FCSTD DOCUMENT  (FreeCAD 0.19R24291 (Git))
Label: Gear_Control_Geometry
License: Creative Commons Attribution-NonCommercial
LicenseURL: http://creativecommons.org/licenses/by-nc/4.0/
objects: TechDraw::DrawViewDimension×9, Sketcher::SketchObject×4, PartDesign::Body×3, TechDraw::DrawViewPart×2, Spreadsheet::Sheet×1, TechDraw::DrawSVGTemplate×1, TechDraw::DrawRichAnno×1, TechDraw::DrawPage×1
note: 7 computed .brp shape members not serialized (recipe doc carries the construction recipe); baked Part::Feature solids carry a one-line shape summary decoded from their .brp

FEATURE [Sketcher::SketchObject] Sketch  label="Frame"
  FullyConstrained = true
  MapMode = 5
  Support = -> [XY_Plane]
  expr: .Constraints.baseLocationX = .Constraints.scale / 2
  expr: .Constraints.baseLocationY = .Constraints.scale / 2
  expr: Constraints[9] = .Constraints.scale
  sketch-geometry (4):
    g0: LineSegment StartX=-107 StartY=107 StartZ=0 EndX=107 EndY=107 EndZ=0
    g1: LineSegment StartX=107 StartY=107 StartZ=0 EndX=107 EndY=-107 EndZ=0
    g2: LineSegment StartX=107 StartY=-107 StartZ=0 EndX=-107 EndY=-107 EndZ=0
    g3: LineSegment StartX=-107 StartY=-107 StartZ=0 EndX=-107 EndY=107 EndZ=0
  constraints (12):
    c: Coincident(g0,g1)
    c: Coincident(g1,g2)
    c: Coincident(g2,g3)
    c: Coincident(g3,g0)
    c: Horizontal(g0)
    c: Horizontal(g2)
    c: Vertical(g1)
    c: Vertical(g3)
    c: DistanceX(g0,g0) = 214  'scale'
    c: DistanceY(g1,g1) = 214
    c: Distance(g0,g-1) = 107  'baseLocationY'
    c: Distance(g0,g-2) = 107  'baseLocationX'
FEATURE [Spreadsheet::Sheet] Spreadsheet
  cells = A1=sepAngule; B1=shiftAngule; A2(sepAngule)==360 / 32; B2(shiftAngle)==sepAngule / 2; A4=points; A5=1; B5(a1)=5.625; A6=2; B6(a2)=16.875; A7=3; B7(a3)=28.125; A8=4; B8(a4)=39.375; A9=5; B9(a5)=50.625; A10=6; B10(a6)=61.875; A11=7; B11(a7)=73.125; A12=8; B12(a8)=84.375; A13=9; B13(a9)=95.625; A14=10; B14(a10)=106.875; A15=11; B15(a11)=118.125; A16=12; B16(a12)=129.375; A17=13; B17(a13)=140.625; A18=14; B18(a14)=151.875; A19=15; B19(a15)=163.125; A20=16; B20(a16)=174.375; A21=17; B21(a17)=185.625; A22=18; B22(a18)=196.875; A23=19; B23(a19)=208.125; A24=20; B24(a20)=219.375; A25=21; B25(a21)=230.625; A26=22; B26(a22)=241.875; A27=23; B27(a23)=253.125; A28=24; B28(a24)=264.375; A29=25; B29(a25)=275.625; A30=26; B30(a26)=286.875; A31=27; B31(a27)=298.125; A32=28; B32(a28)=309.375; A33=29; B33(a29)=320.625; A34=30; B34(a30)=331.875; A35=31; B35(a31)=343.125; A36=32; B36(a32)=354.375
FEATURE [PartDesign::Body] Body001  label="Marker"
  Origin = -> Origin001
FEATURE [Sketcher::SketchObject] Sketch003  label="Positions"
  FullyConstrained = true
  MapMode = 5
  Support = -> [XY_Plane002]
  expr: Constraints[18] = .Constraints.centerPointLenght
  expr: Constraints[19] = .Constraints.centerPointLenght
  expr: Constraints[23] = .Constraints.centerPointLenght
  expr: Constraints[20] = .Constraints.centerPointLenght
  expr: Constraints[21] = .Constraints.centerPointLenght
  expr: Constraints[22] = .Constraints.centerPointLenght
  expr: Constraints[24] = .Constraints.centerPointLenght
  sketch-geometry (16):
    g0: LineSegment StartX=0 StartY=0 StartZ=0 EndX=0 EndY=74 EndZ=0
    g1: GeomPoint X=0 Y=74 Z=0
    g2: LineSegment StartX=0 StartY=0 StartZ=0 EndX=52.3259 EndY=52.3259 EndZ=0
    g3: LineSegment StartX=0 StartY=0 StartZ=0 EndX=-52.3259 EndY=52.3259 EndZ=0
    g4: LineSegment StartX=0 StartY=0 StartZ=0 EndX=74 EndY=0 EndZ=0
    g5: LineSegment StartX=0 StartY=0 StartZ=0 EndX=-74 EndY=0 EndZ=0
    g6: LineSegment StartX=0 StartY=0 StartZ=0 EndX=0 EndY=-74 EndZ=0
    g7: LineSegment StartX=0 StartY=0 StartZ=0 EndX=52.3259 EndY=-52.3259 EndZ=0
    g8: LineSegment StartX=0 StartY=0 StartZ=0 EndX=-52.3259 EndY=-52.3259 EndZ=0
    g9: GeomPoint X=52.3259 Y=52.3259 Z=0
    g10: GeomPoint X=74 Y=0 Z=0
    g11: GeomPoint X=52.3259 Y=-52.3259 Z=0
    g12: GeomPoint X=0 Y=-74 Z=0
    g13: GeomPoint X=-52.3259 Y=-52.3259 Z=0
    g14: GeomPoint X=-74 Y=0 Z=0
    g15: GeomPoint X=-52.3259 Y=52.3259 Z=0
  constraints (32):
    c: Coincident(g0,g-1)
    c: PointOnObject(g0,g-2)
    c: DistanceY(g0,g0) = 74  'centerPointLenght'
    c: Coincident(g1,g0)
    c: Coincident(g2,g-1)
    c: Coincident(g3,g-1)
    c: Coincident(g4,g-1)
    c: PointOnObject(g4,g-1)
    c: Coincident(g5,g-1)
    c: PointOnObject(g5,g-1)
    c: Coincident(g6,g-1)
    c: PointOnObject(g6,g-2)
    c: Coincident(g7,g-1)
    c: Coincident(g8,g-1)
    c: Angle(g8,g6) = 0.785398
    c: Angle(g6,g7) = 0.785398
    c: Angle(g4,g2) = 0.785398
    c: Angle(g3,g5) = 0.785398
    c: Distance(g2) = 74
    c: Distance(g4) = 74
    c: Distance(g7) = 74
    c: Distance(g6) = 74
    c: Distance(g8) = 74
    c: Distance(g5) = 74
    c: Distance(g3) = 74
    c: Coincident(g9,g2)
    c: Coincident(g10,g4)
    c: Coincident(g11,g7)
    c: Coincident(g12,g6)
    c: Coincident(g13,g8)
    c: Coincident(g14,g5)
    c: Coincident(g15,g3)
FEATURE [PartDesign::Body] Body002  label="NumberPosition"
  Group = -> [Sketch003]
  Origin = -> Origin002
FEATURE [TechDraw::DrawSVGTemplate] Template
  Height = 297
  Orientation = 0
  Width = 210
FEATURE [TechDraw::DrawViewPart] View001
  CoarseView = false
  Direction = (0,0,1)
  Focus = 100
  HardHidden = false
  IsoCount = 0
  IsoHidden = false
  IsoVisible = false
  LockPosition = true
  Perspective = false
  Rotation = 0
  ScaleType = 0
  SeamHidden = false
  SeamVisible = true
  SmoothHidden = false
  SmoothVisible = true
  Source = -> [Sketch003]
  X = 105
  XDirection = (1,0,0)
  Y = 148.5
FEATURE [Sketcher::SketchObject] Sketch004  label="Positions001"
  FullyConstrained = true
  MapMode = 5
  Support = -> [XY_Plane]
  expr: Constraints[24] = .Constraints.centerPointLenght
  expr: Constraints[22] = .Constraints.centerPointLenght
  expr: Constraints[21] = .Constraints.centerPointLenght
  expr: Constraints[20] = .Constraints.centerPointLenght
  expr: Constraints[23] = .Constraints.centerPointLenght
  expr: Constraints[19] = .Constraints.centerPointLenght
  expr: Constraints[18] = .Constraints.centerPointLenght
  sketch-geometry (16):
    g0: LineSegment StartX=0 StartY=0 StartZ=0 EndX=0 EndY=74 EndZ=0
    g1: GeomPoint X=0 Y=74 Z=0
    g2: LineSegment StartX=0 StartY=0 StartZ=0 EndX=52.3259 EndY=52.3259 EndZ=0
    g3: LineSegment StartX=0 StartY=0 StartZ=0 EndX=-52.3259 EndY=52.3259 EndZ=0
    g4: LineSegment StartX=0 StartY=0 StartZ=0 EndX=74 EndY=0 EndZ=0
    g5: LineSegment StartX=0 StartY=0 StartZ=0 EndX=-74 EndY=0 EndZ=0
    g6: LineSegment StartX=0 StartY=0 StartZ=0 EndX=0 EndY=-74 EndZ=0
    g7: LineSegment StartX=0 StartY=0 StartZ=0 EndX=52.3259 EndY=-52.3259 EndZ=0
    g8: LineSegment StartX=0 StartY=0 StartZ=0 EndX=-52.3259 EndY=-52.3259 EndZ=0
    g9: GeomPoint X=52.3259 Y=52.3259 Z=0
    g10: GeomPoint X=74 Y=0 Z=0
    g11: GeomPoint X=52.3259 Y=-52.3259 Z=0
    g12: GeomPoint X=0 Y=-74 Z=0
    g13: GeomPoint X=-52.3259 Y=-52.3259 Z=0
    g14: GeomPoint X=-74 Y=0 Z=0
    g15: GeomPoint X=-52.3259 Y=52.3259 Z=0
  constraints (32):
    c: Coincident(g0,g-1)
    c: PointOnObject(g0,g-2)
    c: DistanceY(g0,g0) = 74  'centerPointLenght'
    c: Coincident(g1,g0)
    c: Coincident(g2,g-1)
    c: Coincident(g3,g-1)
    c: Coincident(g4,g-1)
    c: PointOnObject(g4,g-1)
    c: Coincident(g5,g-1)
    c: PointOnObject(g5,g-1)
    c: Coincident(g6,g-1)
    c: PointOnObject(g6,g-2)
    c: Coincident(g7,g-1)
    c: Coincident(g8,g-1)
    c: Angle(g8,g6) = 0.785398
    c: Angle(g6,g7) = 0.785398
    c: Angle(g4,g2) = 0.785398
    c: Angle(g3,g5) = 0.785398
    c: Distance(g2) = 74
    c: Distance(g4) = 74
    c: Distance(g7) = 74
    c: Distance(g6) = 74
    c: Distance(g8) = 74
    c: Distance(g5) = 74
    c: Distance(g3) = 74
    c: Coincident(g9,g2)
    c: Coincident(g10,g4)
    c: Coincident(g11,g7)
    c: Coincident(g12,g6)
    c: Coincident(g13,g8)
    c: Coincident(g14,g5)
    c: Coincident(g15,g3)
FEATURE [Sketcher::SketchObject] Sketch001  label="MainGearSketch"
  ExternalGeometry = -> [Sketch004,Sketch]
  FullyConstrained = true
  MapMode = 5
  Support = -> [XY_Plane]
  expr: Constraints[57] = Spreadsheet.sepAngule
  expr: Constraints[72] = .Constraints.radInt
  expr: Constraints[60] = Spreadsheet.sepAngule
  expr: Constraints[35] = Spreadsheet.sepAngule
  expr: Constraints[33] = Spreadsheet.sepAngule
  expr: Constraints[71] = .Constraints.radInt
  expr: Constraints[69] = .Constraints.radInt
  expr: Constraints[49] = Spreadsheet.sepAngule
  expr: Constraints[58] = Spreadsheet.sepAngule
  expr: Constraints[45] = Spreadsheet.sepAngule
  expr: Constraints[63] = Spreadsheet.sepAngule
  expr: Constraints[112] = .Constraints.radExt
  expr: Constraints[47] = Spreadsheet.sepAngule
  expr: Constraints[111] = .Constraints.radExt
  expr: Constraints[68] = .Constraints.radInt
  expr: Constraints[82] = .Constraints.radExt
  expr: .Constraints.radExt = 91mm
  expr: Constraints[48] = Spreadsheet.sepAngule
  expr: Constraints[64] = Spreadsheet.sepAngule
  expr: Constraints[163] = .Constraints.radExt
  expr: Constraints[110] = .Constraints.radExt
  expr: Constraints[109] = .Constraints.radExt
  expr: Constraints[67] = .Constraints.radInt
  expr: Constraints[43] = Spreadsheet.sepAngule
  expr: .Constraints.p3 = Spreadsheet.sepAngule
  expr: Constraints[34] = Spreadsheet.sepAngule
  expr: .Constraints.p5 = Spreadsheet.sepAngule
  expr: Constraints[26] = Spreadsheet.sepAngule
  expr: Constraints[74] = .Constraints.radInt
  expr: Constraints[32] = Spreadsheet.sepAngule
  expr: Constraints[79] = .Constraints.radExt
  expr: Constraints[78] = .Constraints.radExt
  expr: Constraints[42] = Spreadsheet.sepAngule
  expr: Constraints[81] = .Constraints.radExt
  expr: Constraints[80] = .Constraints.radExt
  expr: .Constraints.p2 = Spreadsheet.sepAngule
  expr: Constraints[61] = Spreadsheet.sepAngule
  expr: .Constraints.p7 = Spreadsheet.sepAngule
  expr: .Constraints.p4 = Spreadsheet.sepAngule
  expr: Constraints[59] = Spreadsheet.sepAngule
  expr: Constraints[73] = .Constraints.radInt
  expr: Constraints[46] = Spreadsheet.sepAngule
  expr: Constraints[27] = Spreadsheet.sepAngule
  expr: Constraints[70] = .Constraints.radInt
  expr: .Constraints.p6 = Spreadsheet.sepAngule
  expr: Constraints[25] = Spreadsheet.sepAngule
  expr: .Constraints.p1 = Spreadsheet.a1
  expr: Constraints[28] = Spreadsheet.sepAngule
  expr: Constraints[30] = Spreadsheet.sepAngule
  expr: Constraints[31] = Spreadsheet.sepAngule
  expr: Constraints[65] = Spreadsheet.sepAngule
  expr: .Constraints.p8 = Spreadsheet.sepAngule
  expr: Constraints[44] = Spreadsheet.sepAngule
  expr: Constraints[29] = Spreadsheet.sepAngule
  expr: Constraints[62] = Spreadsheet.sepAngule
  sketch-geometry (66):
    g0: LineSegment StartX=0 StartY=0 StartZ=0 EndX=0 EndY=91 EndZ=0
    g1: LineSegment StartX=0 StartY=0 StartZ=0 EndX=8.91956 EndY=90.5618 EndZ=0
    g2: LineSegment StartX=0 StartY=0 StartZ=0 EndX=19.8119 EndY=65.3112 EndZ=0
    g3: LineSegment StartX=0 StartY=0 StartZ=0 EndX=32.1728 EndY=60.1911 EndZ=0
    g4: LineSegment StartX=0 StartY=0 StartZ=0 EndX=57.7298 EndY=70.344 EndZ=0
    g5: LineSegment StartX=0 StartY=0 StartZ=0 EndX=70.344 EndY=57.7298 EndZ=0
    g6: LineSegment StartX=0 StartY=0 StartZ=0 EndX=60.1911 EndY=32.1728 EndZ=0
    g7: LineSegment StartX=0 StartY=0 StartZ=0 EndX=65.3112 EndY=19.8119 EndZ=0
    g8: LineSegment StartX=0 StartY=0 StartZ=0 EndX=90.5618 EndY=8.91956 EndZ=0
    g9: LineSegment StartX=0 StartY=0 StartZ=0 EndX=90.5618 EndY=-8.91956 EndZ=0
    g10: LineSegment StartX=0 StartY=0 StartZ=0 EndX=65.3112 EndY=-19.8119 EndZ=0
    g11: LineSegment StartX=0 StartY=0 StartZ=0 EndX=60.1911 EndY=-32.1728 EndZ=0
    g12: LineSegment StartX=0 StartY=0 StartZ=0 EndX=70.344 EndY=-57.7298 EndZ=0
    g13: LineSegment StartX=0 StartY=0 StartZ=0 EndX=57.7298 EndY=-70.344 EndZ=0
    g14: LineSegment StartX=0 StartY=0 StartZ=0 EndX=32.1728 EndY=-60.1911 EndZ=0
    g15: LineSegment StartX=0 StartY=0 StartZ=0 EndX=19.8119 EndY=-65.3112 EndZ=0
    g16: LineSegment StartX=0 StartY=0 StartZ=0 EndX=8.91956 EndY=-90.5618 EndZ=0
    g17: LineSegment StartX=0 StartY=0 StartZ=0 EndX=-8.91956 EndY=-90.5618 EndZ=0
    g18: LineSegment StartX=0 StartY=0 StartZ=0 EndX=-19.8119 EndY=-65.3112 EndZ=0
    g19: LineSegment StartX=0 StartY=0 StartZ=0 EndX=-32.1728 EndY=-60.1911 EndZ=0
    g20: LineSegment StartX=0 StartY=0 StartZ=0 EndX=-57.7298 EndY=-70.344 EndZ=0
    g21: LineSegment StartX=0 StartY=0 StartZ=0 EndX=-70.344 EndY=-57.7298 EndZ=0
    g22: LineSegment StartX=0 StartY=0 StartZ=0 EndX=-60.1911 EndY=-32.1728 EndZ=0
    g23: LineSegment StartX=0 StartY=0 StartZ=0 EndX=-65.3112 EndY=-19.8119 EndZ=0
    g24: LineSegment StartX=0 StartY=0 StartZ=0 EndX=-90.5618 EndY=-8.91956 EndZ=0
    g25: LineSegment StartX=0 StartY=0 StartZ=0 EndX=-90.5618 EndY=8.91956 EndZ=0
    g26: LineSegment StartX=0 StartY=0 StartZ=0 EndX=-65.3112 EndY=19.8119 EndZ=0
    g27: LineSegment StartX=0 StartY=0 StartZ=0 EndX=-60.1911 EndY=32.1728 EndZ=0
    g28: LineSegment StartX=0 StartY=0 StartZ=0 EndX=-70.344 EndY=57.7298 EndZ=0
    g29: LineSegment StartX=0 StartY=0 StartZ=0 EndX=-57.7298 EndY=70.344 EndZ=0
    g30: LineSegment StartX=0 StartY=0 StartZ=0 EndX=-32.1728 EndY=60.1911 EndZ=0
    g31: LineSegment StartX=0 StartY=0 StartZ=0 EndX=-19.8119 EndY=65.3112 EndZ=0
    g32: LineSegment StartX=0 StartY=0 StartZ=0 EndX=-8.91956 EndY=90.5618 EndZ=0
    g33: ArcOfCircle CenterX=-1.16e-13 CenterY=-1.668e-13 CenterZ=0 NormalX=0 NormalY=0 NormalZ=1 AngleXU=0 Radius=68.25 StartAngle=5.79231 EndAngle=5.98866
    g34: ArcOfCircle CenterX=-1.16e-13 CenterY=-1.668e-13 CenterZ=0 NormalX=0 NormalY=0 NormalZ=1 AngleXU=0 Radius=68.25 StartAngle=0.294524 EndAngle=0.490874
    g35: ArcOfCircle CenterX=-1.16e-13 CenterY=-1.668e-13 CenterZ=0 NormalX=0 NormalY=0 NormalZ=1 AngleXU=0 Radius=91 StartAngle=0.687223 EndAngle=0.883573
    g36: ArcOfCircle CenterX=-1.16e-13 CenterY=-1.668e-13 CenterZ=0 NormalX=0 NormalY=0 NormalZ=1 AngleXU=0 Radius=91 StartAngle=6.18501 EndAngle=6.38136
    g37: ArcOfCircle CenterX=-1.16e-13 CenterY=-1.668e-13 CenterZ=0 NormalX=0 NormalY=0 NormalZ=1 AngleXU=0 Radius=91 StartAngle=5.39961 EndAngle=5.59596
    g38: ArcOfCircle CenterX=-1.16e-13 CenterY=-1.668e-13 CenterZ=0 NormalX=0 NormalY=0 NormalZ=1 AngleXU=0 Radius=91 StartAngle=4.61421 EndAngle=4.81056
    g39: ArcOfCircle CenterX=-1.16e-13 CenterY=-1.668e-13 CenterZ=0 NormalX=0 NormalY=0 NormalZ=1 AngleXU=0 Radius=91 StartAngle=3.82882 EndAngle=4.02517
    g40: ArcOfCircle CenterX=-1.16e-13 CenterY=-1.668e-13 CenterZ=0 NormalX=0 NormalY=0 NormalZ=1 AngleXU=0 Radius=91 StartAngle=3.04342 EndAngle=3.23977
    g41: ArcOfCircle CenterX=-1.16e-13 CenterY=-1.668e-13 CenterZ=0 NormalX=0 NormalY=0 NormalZ=1 AngleXU=0 Radius=91 StartAngle=2.25802 EndAngle=2.45437
    g42: ArcOfCircle CenterX=-1.16e-13 CenterY=-1.668e-13 CenterZ=0 NormalX=0 NormalY=0 NormalZ=1 AngleXU=0 Radius=91 StartAngle=1.47262 EndAngle=1.66897
    g43: ArcOfCircle CenterX=-1.16e-13 CenterY=-1.668e-13 CenterZ=0 NormalX=0 NormalY=0 NormalZ=1 AngleXU=0 Radius=68.25 StartAngle=5.00691 EndAngle=5.20326
    g44: ArcOfCircle CenterX=-1.16e-13 CenterY=-1.668e-13 CenterZ=0 NormalX=0 NormalY=0 NormalZ=1 AngleXU=0 Radius=68.25 StartAngle=1.07992 EndAngle=1.27627
    g45: LineSegment StartX=8.91956 StartY=90.5618 StartZ=0 EndX=19.8119 EndY=65.3112 EndZ=0
    g46: LineSegment StartX=32.1728 StartY=60.1911 StartZ=0 EndX=57.7298 EndY=70.344 EndZ=0
    g47: LineSegment StartX=70.344 StartY=57.7298 StartZ=0 EndX=60.1911 EndY=32.1728 EndZ=0
    g48: LineSegment StartX=65.3112 StartY=19.8119 StartZ=0 EndX=90.5618 EndY=8.91956 EndZ=0
    g49: LineSegment StartX=90.5618 StartY=-8.91956 StartZ=0 EndX=65.3112 EndY=-19.8119 EndZ=0
    g50: LineSegment StartX=60.1911 StartY=-32.1728 StartZ=0 EndX=70.344 EndY=-57.7298 EndZ=0
    g51: LineSegment StartX=57.7298 StartY=-70.344 StartZ=0 EndX=32.1728 EndY=-60.1911 EndZ=0
    g52: LineSegment StartX=19.8119 StartY=-65.3112 StartZ=0 EndX=8.91956 EndY=-90.5618 EndZ=0
    g53: LineSegment StartX=-8.91956 StartY=-90.5618 StartZ=0 EndX=-19.8119 EndY=-65.3112 EndZ=0
    g54: LineSegment StartX=-32.1728 StartY=-60.1911 StartZ=0 EndX=-57.7298 EndY=-70.344 EndZ=0
    g55: LineSegment StartX=-70.344 StartY=-57.7298 StartZ=0 EndX=-60.1911 EndY=-32.1728 EndZ=0
    g56: LineSegment StartX=-65.3112 StartY=-19.8119 StartZ=0 EndX=-90.5618 EndY=-8.91956 EndZ=0
    g57: LineSegment StartX=-90.5618 StartY=8.91956 StartZ=0 EndX=-65.3112 EndY=19.8119 EndZ=0
    g58: LineSegment StartX=-60.1911 StartY=32.1728 StartZ=0 EndX=-70.344 EndY=57.7298 EndZ=0
    g59: LineSegment StartX=-57.7298 StartY=70.344 StartZ=0 EndX=-32.1728 EndY=60.1911 EndZ=0
    g60: LineSegment StartX=-19.8119 StartY=65.3112 StartZ=0 EndX=-8.91956 EndY=90.5618 EndZ=0
    g61: ArcOfCircle CenterX=-1.16e-13 CenterY=-1.668e-13 CenterZ=0 NormalX=0 NormalY=0 NormalZ=1 AngleXU=0 Radius=68.25 StartAngle=2.65072 EndAngle=2.84707
    g62: ArcOfCircle CenterX=-1.16e-13 CenterY=-1.668e-13 CenterZ=0 NormalX=0 NormalY=0 NormalZ=1 AngleXU=0 Radius=68.25 StartAngle=3.43612 EndAngle=3.63247
    g63: ArcOfCircle CenterX=-1.16e-13 CenterY=-1.668e-13 CenterZ=0 NormalX=0 NormalY=0 NormalZ=1 AngleXU=0 Radius=68.25 StartAngle=4.22152 EndAngle=4.41786
    g64: ArcOfCircle CenterX=-1.16e-13 CenterY=-1.668e-13 CenterZ=0 NormalX=0 NormalY=0 NormalZ=1 AngleXU=0 Radius=68.25 StartAngle=1.86532 EndAngle=2.06167
    g65: Circle CenterX=-1.16e-13 CenterY=-1.668e-13 CenterZ=0 NormalX=0 NormalY=0 NormalZ=1 AngleXU=0 Radius=17
  constraints (166):
    c: Coincident(g0,g-1)
    c: Vertical(g0)
    c: Coincident(g1,g-1)
    c: Angle(g1,g0) = 0.0981748  'p1'
    c: Coincident(g2,g-1)
    c: Angle(g2,g1) = 0.19635  'p2'
    c: Coincident(g3,g-1)
    c: Angle(g3,g2) = 0.19635  'p3'
    c: Coincident(g4,g-1)
    c: Angle(g4,g3) = 0.19635  'p4'
    c: Coincident(g5,g-1)
    c: Coincident(g6,g-1)
    c: Coincident(g7,g-1)
    c: Coincident(g8,g-1)
    c: Angle(g5,g4) = 0.19635  'p5'
    c: Angle(g6,g5) = 0.19635  'p6'
    c: Angle(g7,g6) = 0.19635  'p7'
    c: Angle(g8,g7) = 0.19635  'p8'
    c: Coincident(g9,g-1)
    c: Coincident(g10,g-1)
    c: Coincident(g11,g-1)
    c: Coincident(g12,g-1)
    c: Coincident(g13,g-1)
    c: Coincident(g14,g-1)
    c: Coincident(g15,g-1)
    c: Coincident(g16,g-1) = 11.25
    c: Angle(g9,g8) = 0.19635
    c: Angle(g10,g9) = 0.19635
    c: Angle(g11,g10) = 0.19635
    c: Angle(g12,g11) = 0.19635
    c: Angle(g13,g12) = 0.19635
    c: Angle(g14,g13) = 0.19635
    c: Angle(g15,g14) = 0.19635
    c: Angle(g16,g15) = 0.19635
    c: Coincident(g17,g-1) = 11.25
    c: Angle(g17,g16) = 0.19635
    c: Coincident(g18,g-1)
    c: Coincident(g19,g-1)
    c: Coincident(g20,g-1)
    c: Coincident(g21,g-1)
    c: Coincident(g22,g-1)
    c: Coincident(g23,g-1)
    c: Coincident(g24,g-1) = 11.25
    c: Angle(g18,g17) = 0.19635
    c: Angle(g19,g18) = 0.19635
    c: Angle(g20,g19) = 0.19635
    c: Angle(g21,g20) = 0.19635
    c: Angle(g22,g21) = 0.19635
    c: Angle(g23,g22) = 0.19635
    c: Angle(g24,g23) = 0.19635
    c: Coincident(g25,g-1)
    c: Coincident(g26,g-1)
    c: Coincident(g27,g-1)
    c: Coincident(g28,g-1)
    c: Coincident(g29,g-1)
    c: Coincident(g30,g-1)
    c: Coincident(g31,g-1)
    c: Coincident(g32,g-1) = 11.25
    c: Angle(g25,g24) = 0.19635
    c: Angle(g26,g25) = 0.19635
    c: Angle(g27,g26) = 0.19635
    c: Angle(g28,g27) = 0.19635
    c: Angle(g29,g28) = 0.19635
    c: Angle(g30,g29) = 0.19635
    c: Angle(g31,g30) = 0.19635
    c: Angle(g32,g31) = 0.19635
    c: Distance(g2) = 68.25  'radInt'
    c: Distance(g3) = 68.25
    c: Distance(g6) = 68.25
    c: Distance(g10) = 68.25
    c: Distance(g14) = 68.25
    c: Distance(g18) = 68.25
    c: Distance(g22) = 68.25
    c: Distance(g26) = 68.25
    c: Distance(g30) = 68.25
    c: Coincident(g33,g10)
    c: Coincident(g33,g11)
    c: Distance(g0) = 91  'radExt'
    c: Distance(g1) = 91
    c: Distance(g4) = 91
    c: Distance(g5) = 91
    c: Distance(g8) = 91
    c: Distance(g12) = 91
    c: Coincident(g34,g33)
    c: Coincident(g34,g7)
    c: Coincident(g34,g6)
    c: Coincident(g35,g33)
    c: Coincident(g35,g5)
    c: Coincident(g35,g4)
    c: Coincident(g36,g33)
    c: Coincident(g36,g9)
    c: Coincident(g36,g8)
    c: Coincident(g37,g33)
    c: Coincident(g37,g12)
    c: Coincident(g37,g13)
    c: Coincident(g38,g33)
    c: Coincident(g38,g16)
    c: Coincident(g38,g17)
    c: Coincident(g39,g33)
    c: Coincident(g39,g20)
    c: Coincident(g39,g21)
    c: Coincident(g40,g33)
    c: Coincident(g40,g24)
    c: Coincident(g40,g25)
    c: Coincident(g41,g33)
    c: Coincident(g41,g28)
    c: Coincident(g41,g29)
    c: Coincident(g42,g33)
    c: Coincident(g42,g1)
    c: Coincident(g42,g32) = 91
    c: Distance(g16) = 91
    c: Distance(g20) = 91
    c: Distance(g24) = 91
    c: Coincident(g43,g33)
    c: Coincident(g43,g14)
    c: Coincident(g43,g15)
    c: Coincident(g44,g33)
    c: Coincident(g44,g2)
    c: Coincident(g44,g3)
    c: Coincident(g45,g42)
    c: Coincident(g45,g44)
    c: Coincident(g46,g44)
    c: Coincident(g46,g35)
    c: Coincident(g47,g35)
    c: Coincident(g47,g34)
    c: Coincident(g48,g34)
    c: Coincident(g48,g36)
    c: Coincident(g49,g36)
    c: Coincident(g49,g33)
    c: Coincident(g50,g33)
    c: Coincident(g50,g37)
    c: Coincident(g51,g37)
    c: Coincident(g51,g43)
    c: Coincident(g52,g43)
    c: Coincident(g52,g38)
    c: Coincident(g53,g38)
    c: Coincident(g53,g18)
    c: Coincident(g54,g19)
    c: Coincident(g54,g39)
    c: Coincident(g55,g39)
    c: Coincident(g55,g22)
    c: Coincident(g56,g23)
    c: Coincident(g56,g40)
    c: Coincident(g57,g40)
    c: Coincident(g57,g26)
    c: Coincident(g58,g27)
    c: Coincident(g58,g41)
    c: Coincident(g59,g41)
    c: Coincident(g59,g30)
    c: Coincident(g60,g31)
    c: Coincident(g60,g42)
    c: Coincident(g61,g33)
    c: Coincident(g61,g58)
    c: Coincident(g61,g57)
    c: Coincident(g62,g33)
    c: Coincident(g62,g56)
    c: Coincident(g62,g55)
    c: Coincident(g63,g33)
    c: Coincident(g63,g53)
    c: Coincident(g63,g54)
    c: Coincident(g64,g33)
    c: Coincident(g64,g59)
    c: Coincident(g64,g60)
    c: Distance(g29) = 91
    c: Coincident(g65,g33)
    c: Radius(g65) = 17
FEATURE [PartDesign::Body] Body  label="GearBody"
  Group = -> [Sketch,Sketch001,Sketch004]
  Origin = -> Origin
FEATURE [TechDraw::DrawViewPart] View
  CoarseView = false
  Direction = (0,0,1)
  Focus = 100
  HardHidden = false
  IsoCount = 0
  IsoHidden = false
  IsoVisible = false
  LockPosition = true
  Perspective = false
  Rotation = 0
  ScaleType = 0
  SeamHidden = false
  SeamVisible = true
  SmoothHidden = false
  SmoothVisible = true
  Source = -> [Sketch001]
  X = 105
  XDirection = (1,0,0)
  Y = 148.5
FEATURE [TechDraw::DrawViewDimension] Dimension007
  Arbitrary = false
  ArbitraryTolerances = false
  EqualTolerance = true
  FormatSpec = R%.1f
  FormatSpecOverTolerance = %+.2f
  FormatSpecUnderTolerance = %+.2f
  Inverted = false
  LockPosition = false
  MeasureType = 1
  OverTolerance = 0
  References2D = -> [View]
  Rotation = 0
  ScaleType = 0
  TheoreticalExact = false
  Type = 4
  UnderTolerance = 0
  X = -24.2186
  Y = 14.5618
FEATURE [TechDraw::DrawViewDimension] Dimension008
  Arbitrary = false
  ArbitraryTolerances = false
  EqualTolerance = true
  FormatSpec = %.3f
  FormatSpecOverTolerance = %+.2f
  FormatSpecUnderTolerance = %+.2f
  Inverted = false
  LockPosition = false
  MeasureType = 1
  OverTolerance = 0
  References2D = -> [View]
  Rotation = 0
  ScaleType = 0
  TheoreticalExact = false
  Type = 7
  UnderTolerance = 0
  X = -12.2972
  Y = 67.2992
FEATURE [TechDraw::DrawViewDimension] Dimension009
  Arbitrary = false
  ArbitraryTolerances = false
  EqualTolerance = true
  FormatSpec = %.2f
  FormatSpecOverTolerance = %+.2f
  FormatSpecUnderTolerance = %+.2f
  Inverted = false
  LockPosition = false
  MeasureType = 1
  OverTolerance = 0
  References2D = -> [View]
  Rotation = 0
  ScaleType = 0
  TheoreticalExact = false
  Type = 7
  UnderTolerance = 0
  X = -12.0707
  Y = 58.0305
FEATURE [TechDraw::DrawViewDimension] Dimension010
  Arbitrary = false
  ArbitraryTolerances = false
  EqualTolerance = true
  FormatSpec = %.2f
  FormatSpecOverTolerance = %+.2f
  FormatSpecUnderTolerance = %+.2f
  Inverted = false
  LockPosition = false
  MeasureType = 1
  OverTolerance = 0
  References2D = -> [View]
  Rotation = 0
  ScaleType = 0
  TheoreticalExact = false
  Type = 7
  UnderTolerance = 0
  X = -5.82433
  Y = 48.5602
FEATURE [TechDraw::DrawViewDimension] Dimension011
  Arbitrary = false
  ArbitraryTolerances = false
  EqualTolerance = true
  FormatSpec = %.2f
  FormatSpecOverTolerance = %+.2f
  FormatSpecUnderTolerance = %+.2f
  Inverted = false
  LockPosition = false
  MeasureType = 1
  OverTolerance = 0
  References2D = -> [View]
  Rotation = 0
  ScaleType = 0
  TheoreticalExact = false
  Type = 7
  UnderTolerance = 0
  X = 6.06386
  Y = 39.09
FEATURE [TechDraw::DrawRichAnno] RichTextAnnotation
  AnnoParent = -> View001
  AnnoText = <!DOCTYPE HTML PUBLIC "-//W3C//DTD HTML 4.0//EN" "http://www.w3.org/TR/REC-html40/strict.dtd">\n<html><head><meta name="qrichtext" content="1" /><style type="text/css">\np, li { white-space: pre-wrap; }\n</style></head><body style=" font-family:'MS Shell Dlg 2'; font-size:8.25pt; font-weight:400; font-style:normal;">\n<p style=" margin-top:0px; margin-bottom:0px; margin-left:0px; margin-right:0px; -qt-block-indent:0; text-indent:0px;"><span style=" font-size:7pt;">Center point for numbers</span></p></body></html>
  LockPosition = false
  MaxWidth = -1
  Rotation = 0
  ScaleType = 0
  ShowFrame = false
  X = 50.1561
  Y = 55.9159
FEATURE [TechDraw::DrawViewDimension] Dimension012
  Arbitrary = false
  ArbitraryTolerances = false
  EqualTolerance = true
  FormatSpec = %.0f
  FormatSpecOverTolerance = %+.2f
  FormatSpecUnderTolerance = %+.2f
  Inverted = false
  LockPosition = false
  MeasureType = 1
  OverTolerance = 0
  References2D = -> [View001]
  Rotation = 0
  ScaleType = 0
  TheoreticalExact = false
  Type = 0
  UnderTolerance = 0
  X = 30.3943
  Y = 24.551
FEATURE [TechDraw::DrawViewDimension] Dimension013
  Arbitrary = false
  ArbitraryTolerances = false
  EqualTolerance = true
  FormatSpec = %.0f
  FormatSpecOverTolerance = %+.2f
  FormatSpecUnderTolerance = %+.2f
  Inverted = false
  LockPosition = false
  MeasureType = 1
  OverTolerance = 0
  References2D = -> [View001]
  Rotation = 0
  ScaleType = 0
  TheoreticalExact = false
  Type = 6
  UnderTolerance = 0
  X = 10.0938
  Y = 27.6048
FEATURE [TechDraw::DrawViewDimension] Dimension
  Arbitrary = false
  ArbitraryTolerances = false
  EqualTolerance = true
  FormatSpec = R%.2f
  FormatSpecOverTolerance = %+.2f
  FormatSpecUnderTolerance = %+.2f
  Inverted = false
  LockPosition = false
  MeasureType = 1
  OverTolerance = 0
  References2D = -> [View]
  Rotation = 0
  ScaleType = 0
  TheoreticalExact = false
  Type = 4
  UnderTolerance = 0
  X = -29.2167
  Y = 77.1725
FEATURE [TechDraw::DrawViewDimension] Dimension014
  Arbitrary = false
  ArbitraryTolerances = false
  EqualTolerance = true
  FormatSpec = R%.0f
  FormatSpecOverTolerance = %+.2f
  FormatSpecUnderTolerance = %+.2f
  Inverted = false
  LockPosition = false
  MeasureType = 1
  OverTolerance = 0
  References2D = -> [View]
  Rotation = 0
  ScaleType = 0
  TheoreticalExact = false
  Type = 4
  UnderTolerance = 0
  X = -72.2108
  Y = 76.1107
FEATURE [TechDraw::DrawPage] Page001  label="GearGeometry"
  KeepUpdated = true
  NextBalloonIndex = 1
  ProjectionType = 1
  Template = -> Template
  Views = -> [View,View001,Dimension007,Dimension008,Dimension009,Dimension010,Dimension011,RichTextAnnotation,Dimension012,Dimension013,Dimension,Dimension014]
